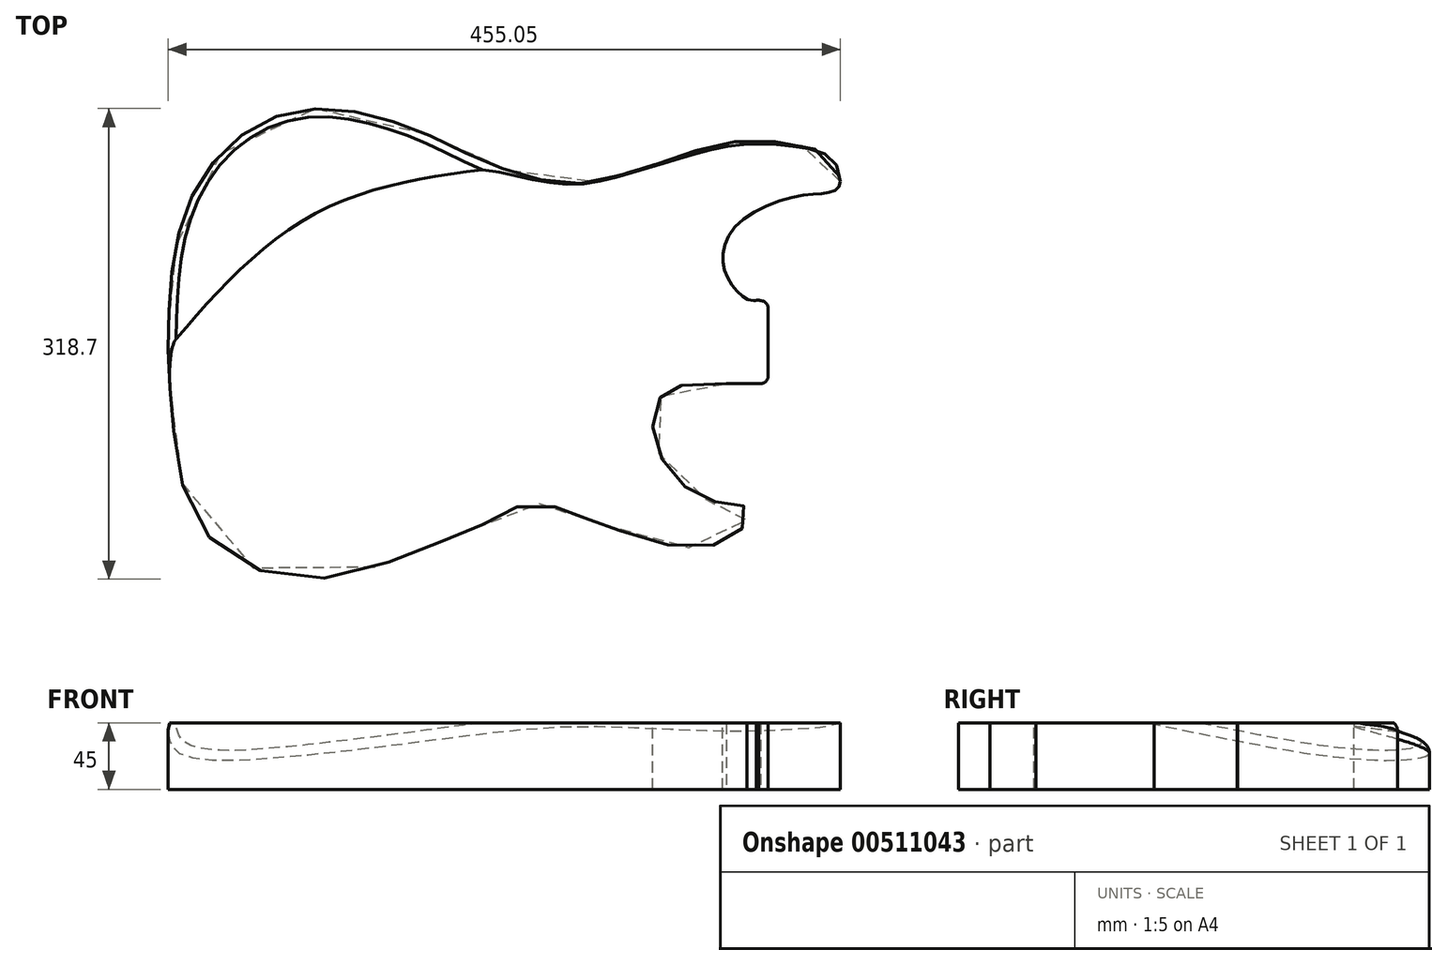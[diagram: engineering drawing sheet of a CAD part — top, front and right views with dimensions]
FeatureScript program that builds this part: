
annotation { "Feature Type Name" : "Feature", "Feature Type Description" : "" }
export const myFeature = defineFeature(function(context is Context, id is Id, definition is map)
    precondition{}
    {
        {
            var Q0;
            Q0=qCreatedBy(makeId("Top.planeOp"),FACE);
            var sketch = newSketch(context, id + "F0", { "sketchPlane" : qUnion([Q0])});
            skLineSegment(sketch, "E0.bottom", {"start": v(-420, 427.06) * mm, "end": v(0, 427.06) * mm});
            skLineSegment(sketch, "E0.top", {"start": v(-420, 107.06) * mm, "end": v(0, 107.06) * mm});
            skLineSegment(sketch, "E0.left", {"start": v(-420, 427.06) * mm, "end": v(-420, 107.06) * mm});
            skLineSegment(sketch, "E0.right", {"start": v(0, 427.06) * mm, "end": v(0, 107.06) * mm});
            skSolve(sketch);
        }
        {
            var Q0;
            Q0=makeQuery(id+"F0.imprint","IMPRINT",FACE,{"disambiguationData":[TD([[makeQuery(id+"F0.imprint","IMPRINT",EDGE,{"derivedFrom":sQuery(id+"F0.wireOp",EDGE,"E0.bottom")}),-1.0]])]});
            var sketch = newSketch(context, id + "F1", { "sketchPlane" : qUnion([Q0])});
            skLineSegment(sketch, "E1.bottom", {"start": v(-21.9, 296.1) * mm, "end": v(-16.95, 296.1) * mm});
            skLineSegment(sketch, "E1.top", {"start": v(-40.16, 239.93) * mm, "end": v(-16.95, 239.93) * mm});
            skLineSegment(sketch, "E1.right", {"start": v(-11.95, 291.1) * mm, "end": v(-11.95, 244.93) * mm});
            skFitSpline(sketch, "E2.trimOffspring", {"points": [v(-418.14, 269.63) * mm, v(-417.3, 245.59) * mm, v(-414.55, 209.96) * mm, v(-395.82, 143.17) * mm, v(-324.66, 107.59) * mm, v(-239.14, 130.68) * mm, v(-200.44, 146.91) * mm, v(-171.1, 158.78) * mm, v(-139.26, 150.04) * mm, v(-119.9, 143.17) * mm, v(-71.84, 129.44) * mm, v(-36.26, 135.68) * mm, v(-26.27, 149.41) * mm, v(-30.64, 158.78) * mm, v(-51.87, 160.65) * mm, v(-73.1, 175) * mm, v(-88.07, 198.1) * mm, v(-88.7, 221.2) * mm, v(-81.2, 234.93) * mm, v(-63.1, 239.3) * mm, v(-20.03, 239.93) * mm, v(-15.66, 242.42) * mm, v(-15.66, 294.86) * mm, v(-21.9, 296.1) * mm, v(-29.4, 299.23) * mm, v(-39.38, 311.71) * mm, v(-42.5, 327.94) * mm, v(-31.27, 349.17) * mm, v(6.57, 366.65) * mm, v(27.76, 369.14) * mm, v(35.7, 372.9) * mm, v(36.59, 381) * mm, v(29.53, 394.11) * mm, v(0, 402.85) * mm, v(-22.56, 404.73) * mm, v(-47.28, 401.6) * mm, v(-82.6, 390.37) * mm, v(-117.02, 379.76) * mm, v(-147.04, 375.39) * mm, v(-199.12, 388.5) * mm, v(-242.38, 408.47) * mm, v(-318.47, 426.18) * mm, v(-379.37, 398.88) * mm, v(-410.46, 343.2) * mm, v(-417.16, 292.85) * mm, v(-418.14, 269.63) * mm]});
            skPoint(sketch, "E1.left.start.orphan", {"position": v(-92.48, 296.1) * mm});
            skPoint(sketch, "E3.visualSharp", {"position": v(-11.95, 296.1) * mm});
            skArc(sketch, "E3.filletArc", {"start": v(-11.95, 291.1) * mm, "mid": v(-13.42, 294.64) * mm, "end": v(-16.95, 296.1) * mm});
            skPoint(sketch, "E4.visualSharp", {"position": v(-11.95, 239.93) * mm});
            skArc(sketch, "E4.filletArc", {"start": v(-16.95, 239.93) * mm, "mid": v(-13.42, 241.4) * mm, "end": v(-11.95, 244.93) * mm});
            skSolve(sketch);
        }
        {
            var Q0;
            Q0 = qSketchRegion(id + "F1", true);
            extrude(context, id + "F2", {"entities" : qUnion([Q0]), "depth" : 45 * mm});
        }
        {
            var Q0;
            Q0=makeQuery(id+"F2.opExtrude","CAP_FACE",FACE,{"disambiguationData":[OSD([sQuery(id+"F1.wireOp",EDGE,"E1.bottom"),sQuery(id+"F1.wireOp",EDGE,"E1.top"),sQuery(id+"F1.wireOp",EDGE,"E1.right"),sQuery(id+"F1.wireOp",EDGE,"E2.trimOffspring"),sQuery(id+"F1.wireOp",EDGE,"E3.filletArc"),sQuery(id+"F1.wireOp",EDGE,"E4.filletArc")])],"isStart":false});
            var sketch = newSketch(context, id + "F3", { "sketchPlane" : qUnion([Q0])});
            skPoint(sketch, "E5.2.internal.orphan", {"position": v(-204.48, 443.38) * mm});
            skPoint(sketch, "E6.1.internal.orphan", {"position": v(-351.22, 537.88) * mm});
            skPoint(sketch, "E6.2.internal.orphan", {"position": v(-215.84, 570.62) * mm});
            skPoint(sketch, "E6.endDerivative.orphan", {"position": v(-263.64, 564.95) * mm});
            skPoint(sketch, "E6.start.orphan", {"position": v(-455.48, 440.69) * mm});
            skPoint(sketch, "E6.startDerivative.orphan", {"position": v(-423.46, 478.46) * mm});
            skFitSpline(sketch, "E7", {"points": [v(-423.41, 257.58) * mm, v(-319.15, 354.78) * mm, v(-183.77, 387.51) * mm], "startDerivative": vector(190.97, 225.32) * mm, "endDerivative": vector(288.5, 34.17) * mm});
            skPoint(sketch, "E8.0.internal.orphan", {"position": v(-445, 296.1) * mm});
            skPoint(sketch, "E8.end.orphan", {"position": v(-204.48, 430.45) * mm});
            skLineSegment(sketch, "E9", {"start": v(-183.77, 387.51) * mm, "end": v(-251.55, 543.25) * mm});
            skLineSegment(sketch, "E10", {"start": v(-251.55, 543.25) * mm, "end": v(-606.3, 445.9) * mm});
            skLineSegment(sketch, "E11", {"start": v(-606.3, 445.9) * mm, "end": v(-423.41, 257.58) * mm});
            skSolve(sketch);
        }
        {
            var Q0;
            Q0=qCreatedBy(makeId("Right.planeOp"),FACE);
            cPlane(context, id + "F4", {"entities" : qUnion([Q0]), "cplaneType" : CPlaneType.OFFSET, "offset" : 415 * mm, "oppositeDirection" : true, "width" : 150 * mm, "height" : 150 * mm});
        }
        {
            var Q0;
            Q0=qCreatedBy(id+"F4.planeOp",FACE);
            var sketch = newSketch(context, id + "F5", { "sketchPlane" : qUnion([Q0])});
            skFitSpline(sketch, "E12", {"points": [v(157.46, 74.6) * mm, v(438.75, 15.43) * mm, v(599.13, -55.75) * mm], "startDerivative": vector(179, -38.69) * mm, "endDerivative": vector(149.92, -173.6) * mm});
            skSolve(sketch);
        }
        {
            var Q0;
            {var subQ0=sQuery(id+"F3.wireOp",EDGE,"E7");var subQ1=sQuery(id+"F1.wireOp",EDGE,"E2.trimOffspring");var subQ2=makeQuery(id+"F0.imprint","IMPRINT",EDGE,{"derivedFrom":sQuery(id+"F0.wireOp",EDGE,"E0.right")});var subQ4=makeQuery(id+"F1.imprint","INTERSECT",VERTEX,{"disambiguationData":[OD(0.0)],"derivedFrom":[subQ2,subQ1]});var subQ5=makeQuery(id+"F2.opExtrude","CAP_EDGE",EDGE,{"disambiguationData":[OSD([subQ1]),TDD([makeQuery(id+"F1.imprint","IMPRINT",EDGE,{"disambiguationData":[TD([[makeQuery(id+"F1.imprint","INTERSECT",VERTEX,{"derivedFrom":[sQuery(id+"F1.wireOp",EDGE,"E1.bottom"),subQ1]}),-1.0]])],"derivedFrom":subQ1}),makeQuery(id+"F1.imprint","IMPRINT",EDGE,{"disambiguationData":[TD([[subQ4,-1.0]])],"derivedFrom":subQ1}),makeQuery(id+"F1.imprint","IMPRINT",EDGE,{"disambiguationData":[TD([[makeQuery(id+"F1.imprint","INTERSECT",VERTEX,{"disambiguationData":[OD(0.0)],"derivedFrom":[sQuery(id+"F1.wireOp",EDGE,"E1.top"),subQ1]}),1.0]])],"derivedFrom":subQ1})])],"isStart":false});var subQ6=makeQuery(id+"F3.imprint","INTERSECT",VERTEX,{"disambiguationData":[OD(0.0)],"derivedFrom":[subQ5,subQ0]});Q0=makeQuery(id+"F3.imprint","IMPRINT",FACE,{"disambiguationData":[TD([[makeQuery(id+"F3.imprint","IMPRINT",EDGE,{"disambiguationData":[TD([[subQ6,-1.0]])],"derivedFrom":subQ0}),1.0]])]});}
            var Q1;
            {var subQ8=sQuery(id+"F3.wireOp",EDGE,"E9");Q1=makeQuery(id+"F3.imprint","IMPRINT",FACE,{"disambiguationData":[TD([[makeQuery(id+"F3.imprint","IMPRINT",EDGE,{"derivedFrom":subQ8}),1.0]])]});}
            var Q2;
            Q2=sQuery(id+"F5.wireOp",EDGE,"E12");
            sweep(context, id + "F6", {"operationType" : NewBodyOperationType.REMOVE, "profiles" : qUnion([Q0, Q1]), "path" : qUnion([Q2]), "keepProfileOrientation" : true});
        }
        {
            var Q0;
            {var subQ0=sQuery(id+"F1.wireOp",EDGE,"E2.trimOffspring");var subQ1=makeQuery(id+"F0.imprint","IMPRINT",EDGE,{"derivedFrom":sQuery(id+"F0.wireOp",EDGE,"E0.right")});var subQ3=makeQuery(id+"F1.imprint","INTERSECT",VERTEX,{"disambiguationData":[OD(0.0)],"derivedFrom":[subQ1,subQ0]});Q0=makeQuery(id+"F6.boolean.opBoolean","INTERSECT",EDGE,{"derivedFrom":[makeQuery(id+"F2.opExtrude","SWEPT_FACE",FACE,{"disambiguationData":[OSD([subQ0]),TDD([makeQuery(id+"F1.imprint","IMPRINT",EDGE,{"disambiguationData":[TD([[makeQuery(id+"F1.imprint","INTERSECT",VERTEX,{"derivedFrom":[sQuery(id+"F1.wireOp",EDGE,"E1.bottom"),subQ0]}),-1.0]])],"derivedFrom":subQ0}),makeQuery(id+"F1.imprint","IMPRINT",EDGE,{"disambiguationData":[TD([[subQ3,-1.0]])],"derivedFrom":subQ0}),makeQuery(id+"F1.imprint","IMPRINT",EDGE,{"disambiguationData":[TD([[makeQuery(id+"F1.imprint","INTERSECT",VERTEX,{"disambiguationData":[OD(0.0)],"derivedFrom":[sQuery(id+"F1.wireOp",EDGE,"E1.top"),subQ0]}),1.0]])],"derivedFrom":subQ0})])]}),makeQuery(id+"F6.opSweep","SWEPT_FACE",FACE,{"disambiguationData":[OSD([sQuery(id+"F3.wireOp",EDGE,"E7"),sQuery(id+"F5.wireOp",EDGE,"E12")])]})]});}
            fillet(context, id + "F7", {"entities" : qUnion([Q0]), "radius" : 7 * mm, "tangentPropagation" : true, "allowEdgeOverflow" : false});
        }
    });
